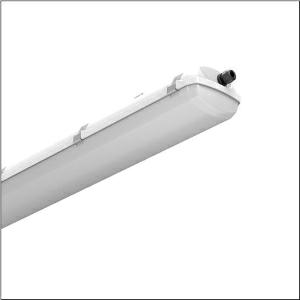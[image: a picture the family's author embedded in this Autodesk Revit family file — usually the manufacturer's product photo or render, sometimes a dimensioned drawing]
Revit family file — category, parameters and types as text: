
# Revit family: monsun_r__ex_51fxa27l440a_d3da
name_source: partatom
category: Lighting Fixtures
units: mm (PartAtom-declared; Revit-internal decimal feet)

## family parameters
Cut with Voids When Loaded = No
Host = Face
Light Source = No
Part Type = Normal
Room Calculation Point = No
Round Connector Dimension = Use Diameter
Shared = No

## types (1)
- Monsun® Ex (1 x LED, 4650 lm, 30 W, 4000K)
    Apparent Load = 30 VA
    CIE Flux Codes = 46 76 94 98 100
    Color Rendering = 80
    Color Temperature = 4000K
    Default Elevation = 1800 mm
    Description = Monsun® Ex, damp-proof luminaire, primary optical cover: cover, of PC, UV-stabilised, opal, light emission: direct distribution, primary light characteristic: symmetric, installation type: surface-mounted, LED, rated luminous flux: 4.650lm, luminous efficacy: 155lm/W, light colour: 840, colour temperature: 4000K, control gear: ECG, with terminal, 3-pole, max. 2.5mm², through-wiring: 5x 2.5mm², mains connection: 220..250V, AC, 50/60Hz, rated input power: 30W, housing, of PC, light grey (RAL 7035), incl. 1x Ex cable gland M20 for cable diameter 7..12mm with sealing, incl. 1x Ex locking screw M20 with sealing, length: 1.280mm, width: 155mm, height: 105mm, clip for enclosure, of stainless steel, protection rating (complete): IP66, insulation class (complete): insulation class I (protective earthing), certification: CE, explosion class: zone 1,21 II 2G Ex eb mb op is IIC T4 Gb, II 2D Ex tb op is IIIC T67°C Db, impact resistance: IK10, permissible operating ambient temperature: -20..+40°C, contact your sales advisor before using the luminaires in applications with unclear chemical exposure, large temperature fluctuations or condensation-forming humidity, packaging unit: 1 piece
    Height = 105 mm
    Lamp = 1 x LED
    Lamp Light Flux = 4650 lm
    Lamp Power = 30 W
    Lamp count = 1
    Length = 1280 mm
    Luminous efficacy = 155 lm/W
    Manufacturer = Siteco
    ModVariant = No
    Model = 51FXA27L440A
    Mounting Place = Ceiling
    Mounting Type = Surface mounted
    Number of Poles = 1
    OnlyDefault = Yes
    Power Factor = 1
    Product Name = Monsun® Ex
    Product group = damp-proof luminaire
    ProductGroupID = 301
    Protection Class = Protection class I
    Protection Degree = IP 66
    RLX_Detail_Level = 1
    RLX_Emergency_Light_Flux = 0 lm
    RLX_Emergency_Type = 0
    RLX_Emergency_Type_DB = No
    RlxData = <blob elided: 41645 chars, md5=3787bf12>
    Socket = socket
    Standby Power = 0 W
    System Light Flux = 4650 lm
    System Power = 30 W
    Type Comments = Product without accessories
    Type Image = l_1258882.jpg
    URL = http://relux.com
    VarID = ---
    Voltage = 0 V
    Weight = 0.00 kg
    Width = 155 mm

## geometry (parser evidence)
native form markers: Blend x4, Sweep x11
no freeform markers — native parametric forms only
